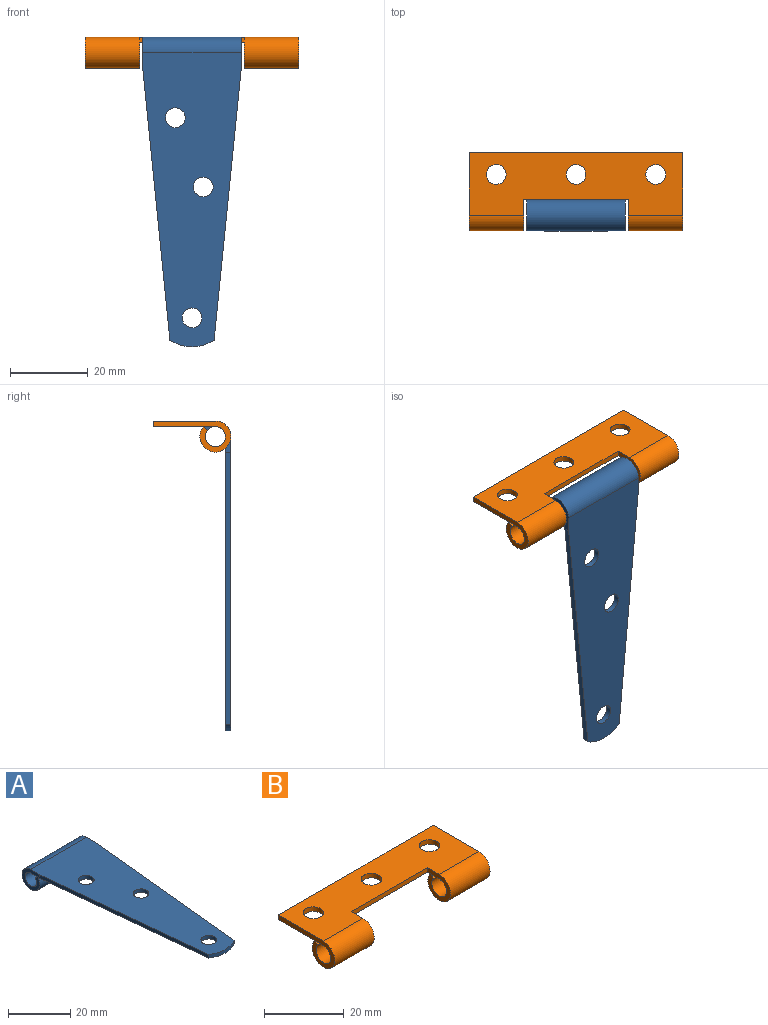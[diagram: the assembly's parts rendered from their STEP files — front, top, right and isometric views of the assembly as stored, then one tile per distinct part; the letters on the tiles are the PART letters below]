
ASSEMBLY  parts=2 mates=1
PART A: 13 faces, bbox 25.4x79.9x8 mm
  f0: plane 8.14x8mm, normal (1,0,0), area 30.8mm2, adj f7,f8,f9,f10,f11,f12
  f1: plane 8.14x8mm, normal (-1,0,0), area 30.8mm2, adj f2,f8,f9,f10,f11,f12
  f2: plane 70x6.99mm, normal (-1,-0.1,0), area 98.3mm2, adj f1,f3,f8,f9
  f3: cylinder r=10.07mm len=11.43mm, axis (0,0,1), area 17mm2, adj f2,f7,f8,f9
  f4: cylinder r=2.55mm len=5.11mm, axis (0,0,1), area 22.4mm2, adj f8,f9
  f5: cylinder r=2.55mm len=5.11mm, axis (0,0,1), area 22.4mm2, adj f8,f9
  f6: cylinder r=2.55mm len=5.11mm, axis (0,0,1), area 22.4mm2, adj f8,f9
  f7: plane 70x6.99mm, normal (1,-0.1,0), area 98.3mm2, adj f0,f3,f8,f9
  f8: plane 75.92x25.4mm, normal (0,0,-1), area 1346.6mm2, adj f0,f1,f2,f3,f4,f5,f6,f7
  f9: plane 75.92x25.4mm, normal (0,0,1), area 1346.6mm2, adj f0,f1,f2,f3,f4,f5,f6,f7
  f10: plane 25.4x1.07mm, normal (0,0.64,0.76), area 35.5mm2, adj f0,f1,f11,f12
  f11: cylinder r=4mm len=25.4mm, axis (-1,0,0), area 550mm2, adj f0,f1,f9,f10
  f12: cylinder r=2.6mm len=25.4mm, axis (-1,0,0), area 357.9mm2, adj f0,f1,f8,f10
PART B: 17 faces, bbox 55x20.1x8 mm
  f0: plane 14x1.07mm, normal (0,-0.64,0.76), area 19.6mm2, adj f1,f2,f3,f8
  f1: cylinder r=2.6mm len=14mm, axis (-1,0,0), area 197.3mm2, adj f0,f3,f8,f12
  f2: cylinder r=4mm len=14mm, axis (-1,0,0), area 303.2mm2, adj f0,f3,f8,f13
  f3: plane 8.14x8mm, normal (1,0,0), area 30.8mm2, adj f0,f1,f2,f4,f12,f13
  f4: plane 26.99x1.4mm, normal (0,-1,0), area 37.7mm2, adj f3,f5,f12,f13
  f5: plane 8.14x8mm, normal (-1,0,0), area 30.8mm2, adj f4,f12,f13,f14,f15,f16
  f6: plane 20.08x8mm, normal (1,0,0), area 47.4mm2, adj f7,f12,f13,f14,f15,f16
  f7: plane 54.99x1.4mm, normal (0,1,0), area 76.8mm2, adj f6,f8,f12,f13
  f8: plane 20.08x8mm, normal (-1,0,0), area 47.4mm2, adj f0,f1,f2,f7,f12,f13
  f9: cylinder r=2.55mm len=5.11mm, axis (0,0,1), area 22.4mm2, adj f12,f13
  f10: cylinder r=2.55mm len=5.11mm, axis (0,0,1), area 22.4mm2, adj f12,f13
  f11: cylinder r=2.55mm len=5.11mm, axis (0,0,1), area 22.4mm2, adj f12,f13
  f12: plane 54.99x16.08mm, normal (0,0,-1), area 711mm2, adj f1,f3,f4,f5,f6,f7,f8,f9
  f13: plane 54.99x16.08mm, normal (0,0,1), area 711mm2, adj f2,f3,f4,f5,f6,f7,f8,f9
  f14: cylinder r=2.6mm len=14mm, axis (-1,0,0), area 197.3mm2, adj f5,f6,f12,f16
  f15: cylinder r=4mm len=14mm, axis (-1,0,0), area 303.2mm2, adj f5,f6,f13,f16
  f16: plane 14x1.07mm, normal (0,-0.64,0.76), area 19.6mm2, adj f5,f6,f14,f15
PLACE A rot(axis=(1,0,0),90deg) t=(-13.47,-15.23,-14.37)mm
PLACE B t=(-13.47,-11.23,-10.37)mm fixed
MATE revolute B.f1 <-> A.f11  axis (-1,0,0) through (-13.47,-11.23,-14.37)mm
